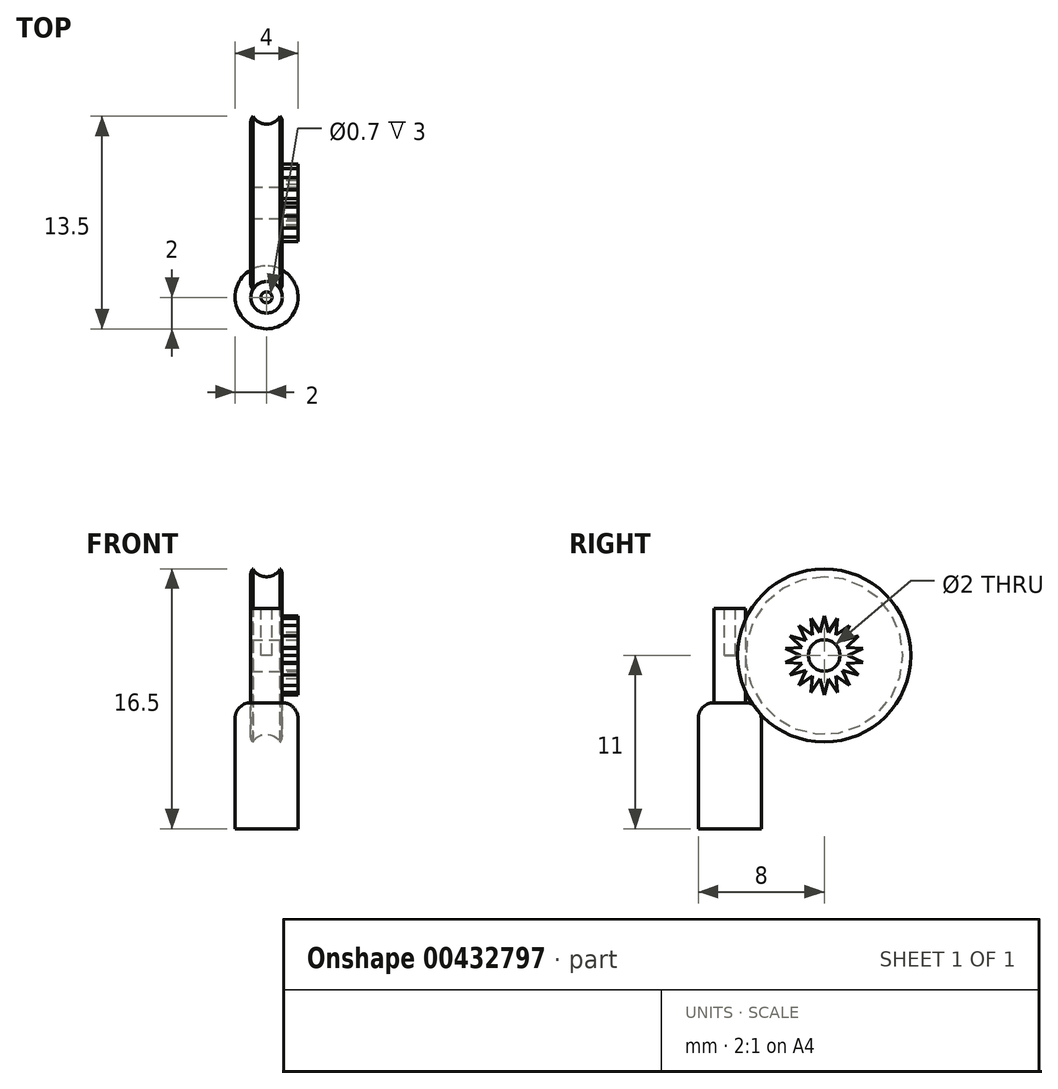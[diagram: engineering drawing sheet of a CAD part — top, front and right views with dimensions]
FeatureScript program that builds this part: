
annotation { "Feature Type Name" : "Feature", "Feature Type Description" : "" }
export const myFeature = defineFeature(function(context is Context, id is Id, definition is map)
    precondition{}
    {
        {
            var Q0;
            Q0=qCreatedBy(makeId("Top.planeOp"),FACE);
            var sketch = newSketch(context, id + "F0", { "sketchPlane" : qUnion([Q0])});
            skCircle(sketch, "E0", {"center": v(0, 0) * mm, "radius": 2 * mm});
            skSolve(sketch);
        }
        {
            var Q0;
            Q0=makeQuery(id+"F0.imprint","IMPRINT",FACE,{"disambiguationData":[TD([[makeQuery(id+"F0.imprint","IMPRINT",EDGE,{"derivedFrom":sQuery(id+"F0.wireOp",EDGE,"E0")}),1.0]])]});
            extrude(context, id + "F1", {"entities" : qUnion([Q0]), "depth" : 8 * mm});
        }
        {
            var Q0;
            Q0=makeQuery(id+"F1.opExtrude","CAP_EDGE",EDGE,{"disambiguationData":[OSD([sQuery(id+"F0.wireOp",EDGE,"E0")])],"isStart":false});
            fillet(context, id + "F2", {"entities" : qUnion([Q0]), "radius" : 1 * mm, "tangentPropagation" : true, "allowEdgeOverflow" : false});
        }
        {
            var Q0;
            Q0=makeQuery(id+"F1.opExtrude","CAP_FACE",FACE,{"disambiguationData":[OSD([sQuery(id+"F0.wireOp",EDGE,"E0")])],"isStart":false});
            var sketch = newSketch(context, id + "F3", { "sketchPlane" : qUnion([Q0])});
            skCircle(sketch, "E1", {"center": v(0, 0) * mm, "radius": 1 * mm});
            skSolve(sketch);
        }
        {
            var Q0;
            Q0=makeQuery(id+"F3.imprint","IMPRINT",FACE,{"disambiguationData":[TD([[makeQuery(id+"F3.imprint","IMPRINT",EDGE,{"derivedFrom":sQuery(id+"F3.wireOp",EDGE,"E1")}),1.0]])]});
            extrude(context, id + "F4", {"entities" : qUnion([Q0]), "operationType" : NewBodyOperationType.ADD, "depth" : 3 * mm});
        }
        {
            var Q0;
            Q0=makeQuery(id+"F4.opExtrude","CAP_FACE",FACE,{"disambiguationData":[OSD([sQuery(id+"F3.wireOp",EDGE,"E1")])],"isStart":false});
            var sketch = newSketch(context, id + "F5", { "sketchPlane" : qUnion([Q0])});
            skArc(sketch, "E2", {"start": v(-0.87, 0.5) * mm, "mid": v(0, 1) * mm, "end": v(0.87, 0.5) * mm});
            skLineSegment(sketch, "E3", {"start": v(-1, 0.5) * mm, "end": v(-1, 6) * mm});
            skLineSegment(sketch, "E4", {"start": v(1, 0.5) * mm, "end": v(1, 6) * mm});
            skLineSegment(sketch, "E5", {"start": v(-1, 6) * mm, "end": v(1, 6) * mm});
            skLineSegment(sketch, "E6", {"start": v(1, 0.5) * mm, "end": v(0.87, 0.5) * mm});
            skPoint(sketch, "E7.orphan", {"position": v(1, 0) * mm});
            skLineSegment(sketch, "E8.trimOffspring", {"start": v(-0.87, 0.5) * mm, "end": v(-1, 0.5) * mm});
            skSolve(sketch);
        }
        {
            var Q0;
            Q0=makeQuery(id+"F5.imprint","IMPRINT",FACE,{"disambiguationData":[TD([[makeQuery(id+"F5.imprint","IMPRINT",EDGE,{"derivedFrom":sQuery(id+"F5.wireOp",EDGE,"E2")}),-1.0]])]});
            var Q1;
            Q1=sQuery(id+"F5.wireOp",EDGE,"E5");
            revolve(context, id + "F6", {"entities" : qUnion([Q0]), "axis" : qUnion([Q1]), "revolveType" : RevolveType.FULL});
        }
        {
            var Q0;
            Q0=makeQuery(id+"F6.opRevolve","SWEPT_EDGE",EDGE,{"disambiguationData":[OSD([sQuery(id+"F5.wireOp",EDGE,"E4"),sQuery(id+"F5.wireOp",EDGE,"E6")])]});
            var Q1;
            Q1=makeQuery(id+"F6.opRevolve","SWEPT_EDGE",EDGE,{"disambiguationData":[OSD([sQuery(id+"F5.wireOp",EDGE,"E3"),sQuery(id+"F5.wireOp",EDGE,"E8.trimOffspring")])]});
            fillet(context, id + "F7", {"entities" : qUnion([Q0, Q1]), "radius" : .5 * mm, "tangentPropagation" : true, "allowEdgeOverflow" : false});
        }
        {
            var Q0;
            Q0=makeQuery(id+"F6.opRevolve","SWEPT_FACE",FACE,{"disambiguationData":[OSD([sQuery(id+"F5.wireOp",EDGE,"E4")])]});
            var sketch = newSketch(context, id + "F8", { "sketchPlane" : qUnion([Q0])});
            skCircle(sketch, "E9", {"center": v(6, 11) * mm, "radius": 1 * mm});
            skSolve(sketch);
        }
        {
            var Q0;
            Q0 = qSketchRegion(id + "F8", true);
            extrude(context, id + "F9", {"entities" : qUnion([Q0]), "operationType" : NewBodyOperationType.REMOVE, "endBound" : BoundingType.THROUGH_ALL, "oppositeDirection" : true, "depth" : 25 * mm});
        }
        {
            var Q0;
            Q0=makeQuery(id+"F4.opExtrude","CAP_FACE",FACE,{"disambiguationData":[OSD([sQuery(id+"F3.wireOp",EDGE,"E1")])],"isStart":false});
            var sketch = newSketch(context, id + "F10", { "sketchPlane" : qUnion([Q0])});
            skCircle(sketch, "E10", {"center": v(0, 0) * mm, "radius": 1 * mm});
            skSolve(sketch);
        }
        {
            var Q0;
            Q0 = qSketchRegion(id + "F10", true);
            extrude(context, id + "F11", {"entities" : qUnion([Q0]), "operationType" : NewBodyOperationType.ADD, "depth" : 3 * mm});
        }
        {
            var Q0;
            Q0=makeQuery(id+"F11.opExtrude","CAP_FACE",FACE,{"disambiguationData":[OSD([sQuery(id+"F10.wireOp",EDGE,"E10")])],"isStart":false});
            var sketch = newSketch(context, id + "F12", { "sketchPlane" : qUnion([Q0])});
            skCircle(sketch, "E11", {"center": v(0, 0) * mm, "radius": 0.35 * mm});
            skSolve(sketch);
        }
        {
            var Q0;
            Q0 = qSketchRegion(id + "F12", true);
            extrude(context, id + "F13", {"entities" : qUnion([Q0]), "operationType" : NewBodyOperationType.REMOVE, "oppositeDirection" : true, "depth" : 3 * mm});
        }
        {
            var Q0;
            Q0=makeQuery(id+"F6.opRevolve","SWEPT_FACE",FACE,{"disambiguationData":[OSD([sQuery(id+"F5.wireOp",EDGE,"E4")])]});
            var sketch = newSketch(context, id + "F14", { "sketchPlane" : qUnion([Q0])});
            skCircle(sketch, "E12", {"center": v(6, 11) * mm, "radius": 1 * mm});
            skCircle(sketch, "E13", {"center": v(6, 11) * mm, "radius": 2.5 * mm, "construction": true});
            skLineSegment(sketch, "E14", {"start": v(6, 11) * mm, "end": v(6, 14.61) * mm});
            skLineSegment(sketch, "E15", {"start": v(6, 14.61) * mm, "end": v(6, 11) * mm});
            skLineSegment(sketch, "E16", {"start": v(6, 11) * mm, "end": v(6.86, 15.88) * mm, "construction": true});
            skLineSegment(sketch, "E17", {"start": v(6, 11) * mm, "end": v(4.9, 17.19) * mm, "construction": true});
            skCircle(sketch, "E18", {"center": v(6, 11) * mm, "radius": 1.5 * mm, "construction": true});
            skLineSegment(sketch, "E19", {"start": v(5.74, 12.48) * mm, "end": v(6, 13.5) * mm});
            skLineSegment(sketch, "E20", {"start": v(6, 13.5) * mm, "end": v(6.26, 12.48) * mm});
            skLineSegment(sketch, "E21.1.0", {"start": v(5.14, 13.35) * mm, "end": v(5.74, 12.48) * mm});
            skLineSegment(sketch, "E21.1.1", {"start": v(5.25, 12.3) * mm, "end": v(5.14, 13.35) * mm});
            skLineSegment(sketch, "E21.2.0", {"start": v(4.4, 12.92) * mm, "end": v(5.25, 12.3) * mm});
            skLineSegment(sketch, "E21.2.1", {"start": v(4.85, 11.96) * mm, "end": v(4.4, 12.92) * mm});
            skLineSegment(sketch, "E21.3.0", {"start": v(3.83, 12.25) * mm, "end": v(4.85, 11.96) * mm});
            skLineSegment(sketch, "E21.3.1", {"start": v(4.6, 11.51) * mm, "end": v(3.83, 12.25) * mm});
            skLineSegment(sketch, "E21.4.0", {"start": v(3.54, 11.43) * mm, "end": v(4.6, 11.51) * mm});
            skLineSegment(sketch, "E21.4.1", {"start": v(4.5, 11) * mm, "end": v(3.54, 11.43) * mm});
            skLineSegment(sketch, "E21.5.0", {"start": v(3.54, 10.57) * mm, "end": v(4.5, 11) * mm});
            skLineSegment(sketch, "E21.5.1", {"start": v(4.6, 10.49) * mm, "end": v(3.54, 10.57) * mm});
            skLineSegment(sketch, "E21.6.0", {"start": v(3.83, 9.75) * mm, "end": v(4.6, 10.49) * mm});
            skLineSegment(sketch, "E21.6.1", {"start": v(4.85, 10.04) * mm, "end": v(3.83, 9.75) * mm});
            skLineSegment(sketch, "E21.7.0", {"start": v(4.4, 9.08) * mm, "end": v(4.85, 10.04) * mm});
            skLineSegment(sketch, "E21.7.1", {"start": v(5.25, 9.7) * mm, "end": v(4.4, 9.08) * mm});
            skLineSegment(sketch, "E21.8.0", {"start": v(5.14, 8.65) * mm, "end": v(5.25, 9.7) * mm});
            skLineSegment(sketch, "E21.8.1", {"start": v(5.74, 9.52) * mm, "end": v(5.14, 8.65) * mm});
            skLineSegment(sketch, "E21.9.0", {"start": v(6, 8.5) * mm, "end": v(5.74, 9.52) * mm});
            skLineSegment(sketch, "E21.9.1", {"start": v(6.26, 9.52) * mm, "end": v(6, 8.5) * mm});
            skLineSegment(sketch, "E21.10.0", {"start": v(6.86, 8.65) * mm, "end": v(6.26, 9.52) * mm});
            skLineSegment(sketch, "E21.10.1", {"start": v(6.75, 9.7) * mm, "end": v(6.86, 8.65) * mm});
            skLineSegment(sketch, "E21.11.0", {"start": v(7.6, 9.08) * mm, "end": v(6.75, 9.7) * mm});
            skLineSegment(sketch, "E21.11.1", {"start": v(7.15, 10.04) * mm, "end": v(7.6, 9.08) * mm});
            skLineSegment(sketch, "E21.12.0", {"start": v(8.17, 9.75) * mm, "end": v(7.15, 10.04) * mm});
            skLineSegment(sketch, "E21.12.1", {"start": v(7.4, 10.49) * mm, "end": v(8.17, 9.75) * mm});
            skLineSegment(sketch, "E21.13.0", {"start": v(8.46, 10.57) * mm, "end": v(7.4, 10.49) * mm});
            skLineSegment(sketch, "E21.13.1", {"start": v(7.5, 11) * mm, "end": v(8.46, 10.57) * mm});
            skLineSegment(sketch, "E21.14.0", {"start": v(8.46, 11.43) * mm, "end": v(7.5, 11) * mm});
            skLineSegment(sketch, "E21.14.1", {"start": v(7.4, 11.51) * mm, "end": v(8.46, 11.43) * mm});
            skLineSegment(sketch, "E21.15.0", {"start": v(8.17, 12.25) * mm, "end": v(7.4, 11.51) * mm});
            skLineSegment(sketch, "E21.15.1", {"start": v(7.15, 11.96) * mm, "end": v(8.17, 12.25) * mm});
            skLineSegment(sketch, "E21.16.0", {"start": v(7.6, 12.92) * mm, "end": v(7.15, 11.96) * mm});
            skLineSegment(sketch, "E21.16.1", {"start": v(6.75, 12.3) * mm, "end": v(7.6, 12.92) * mm});
            skLineSegment(sketch, "E21.17.0", {"start": v(6.86, 13.35) * mm, "end": v(6.75, 12.3) * mm});
            skLineSegment(sketch, "E21.17.1", {"start": v(6.26, 12.48) * mm, "end": v(6.86, 13.35) * mm});
            skSolve(sketch);
        }
        {
            var Q0;
            Q0 = qSketchRegion(id + "F14", true);
            extrude(context, id + "F15", {"entities" : qUnion([Q0]), "operationType" : NewBodyOperationType.ADD, "depth" : 1 * mm});
        }
    });
